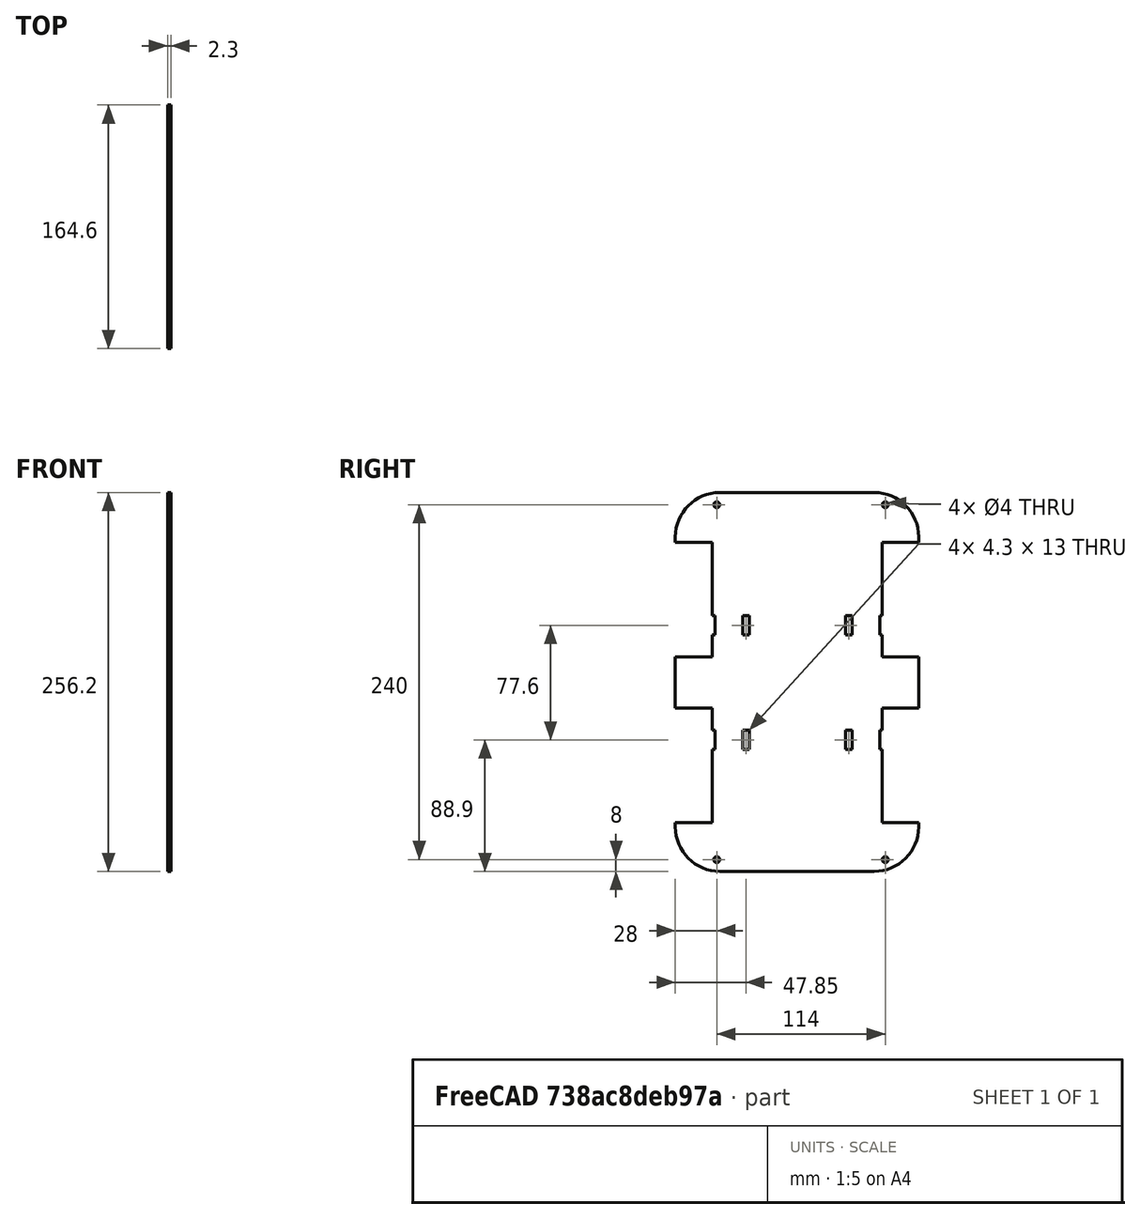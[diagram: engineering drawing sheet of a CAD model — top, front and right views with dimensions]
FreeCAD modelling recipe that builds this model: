
FCSTD DOCUMENT  (FreeCAD 0.17R13522 (Git))
Label: chasis_inferior
License: All rights reserved
LicenseURL: http://en.wikipedia.org/wiki/All_rights_reserved
objects: Part::Cut×16, Part::Box×13, Part::Fillet×4, Part::Cylinder×4
note: 37 computed .brp shape members not serialized (recipe doc carries the construction recipe); baked Part::Feature solids carry a one-line shape summary decoded from their .brp

FEATURE [Part::Box] Box  label="Cubo"
  AttacherType = Attacher::AttachEngine3D
  Height = 256.2
  Length = 2.3
  Width = 164.6
FEATURE [Part::Box] Box001  label="Cubo001"
  AttacherType = Attacher::AttachEngine3D
  Height = 77.4
  Length = 10
  Placement = pos=(0,0,33) rot=(0,0,1;0rad)
  Width = 25
FEATURE [Part::Box] Box002  label="Cubo002"
  AttacherType = Attacher::AttachEngine3D
  Height = 77.4
  Length = 10
  Placement = pos=(0,0,145) rot=(0,0,1;0rad)
  Width = 25
FEATURE [Part::Box] Box003  label="Cubo003"
  AttacherType = Attacher::AttachEngine3D
  Height = 77.4
  Length = 10
  Placement = pos=(0,140,33) rot=(0,0,1;0rad)
  Width = 25
FEATURE [Part::Cut] Cut
  Base = -> Box
  Tool = -> Box003
FEATURE [Part::Cut] Cut001
  Base = -> Cut
  Tool = -> Box001
FEATURE [Part::Box] Box004  label="Cubo004"
  AttacherType = Attacher::AttachEngine3D
  Height = 77.4
  Length = 10
  Placement = pos=(0,140,145) rot=(0,0,1;0rad)
  Width = 25
FEATURE [Part::Cut] Cut002
  Base = -> Cut001
  Tool = -> Box004
FEATURE [Part::Cut] Cut003
  Base = -> Cut002
  Tool = -> Box002
FEATURE [Part::Fillet] Fillet
  Base = -> Cut003
  Edges = 1 edges r=30: [Edge29]
FEATURE [Part::Fillet] Fillet001
  Base = -> Fillet
  Edges = 1 edges r=30: [Edge23]
FEATURE [Part::Fillet] Fillet002
  Base = -> Fillet001
  Edges = 1 edges r=30: [Edge63]
FEATURE [Part::Fillet] Fillet003
  Base = -> Fillet002
  Edges = 1 edges r=30: [Edge31]
FEATURE [Part::Box] Box005  label="Cubo005"
  AttacherType = Attacher::AttachEngine3D
  Height = 13
  Length = 10
  Placement = pos=(-2,25,82.4) rot=(0,0,1;0rad)
  Width = 1.8
FEATURE [Part::Box] Box006  label="Cubo006"
  AttacherType = Attacher::AttachEngine3D
  Height = 13
  Length = 10
  Placement = pos=(0,45.7,82.4) rot=(0,0,1;0rad)
  Width = 4.3
FEATURE [Part::Box] Box007  label="Cubo007"
  AttacherType = Attacher::AttachEngine3D
  Height = 13
  Length = 10
  Placement = pos=(-2,138.2,82.4) rot=(0,0,1;0rad)
  Width = 1.8
FEATURE [Part::Cut] Cut004
  Base = -> Fillet003
  Tool = -> Box005
FEATURE [Part::Box] Box008  label="Cubo008"
  AttacherType = Attacher::AttachEngine3D
  Height = 13
  Length = 10
  Placement = pos=(0,45.7,160) rot=(0,0,1;0rad)
  Width = 4.3
FEATURE [Part::Cut] Cut005
  Base = -> Cut004
  Tool = -> Box006
FEATURE [Part::Box] Box009  label="Cubo009"
  AttacherType = Attacher::AttachEngine3D
  Height = 13
  Length = 10
  Placement = pos=(-2,115.2,82.4) rot=(0,0,1;0rad)
  Width = 4.3
FEATURE [Part::Box] Box010  label="Cubo010"
  AttacherType = Attacher::AttachEngine3D
  Height = 13
  Length = 10
  Placement = pos=(-2,25,160) rot=(0,0,1;0rad)
  Width = 1.8
FEATURE [Part::Cut] Cut006
  Base = -> Cut005
  Tool = -> Box010
FEATURE [Part::Cut] Cut007
  Base = -> Cut006
  Tool = -> Box008
FEATURE [Part::Box] Box011  label="Cubo011"
  AttacherType = Attacher::AttachEngine3D
  Height = 13
  Length = 10
  Placement = pos=(-2,138.2,160) rot=(0,0,1;0rad)
  Width = 1.8
FEATURE [Part::Box] Box012  label="Cubo012"
  AttacherType = Attacher::AttachEngine3D
  Height = 13
  Length = 10
  Placement = pos=(-2,115.2,160) rot=(0,0,1;0rad)
  Width = 4.3
FEATURE [Part::Cut] Cut008
  Base = -> Cut007
  Tool = -> Box009
FEATURE [Part::Cut] Cut009
  Base = -> Cut008
  Tool = -> Box007
FEATURE [Part::Cut] Cut010
  Base = -> Cut009
  Tool = -> Box011
FEATURE [Part::Cut] Cut011
  Base = -> Cut010
  Tool = -> Box012
FEATURE [Part::Cylinder] Cylinder  label="Cilindro"
  Angle = 360
  AttacherType = Attacher::AttachEngine3D
  Height = 10
  Placement = pos=(-2,28,8) rot=(0,1,0;1.5708rad)
  Radius = 2
FEATURE [Part::Cylinder] Cylinder001  label="Cilindro001"
  Angle = 360
  AttacherType = Attacher::AttachEngine3D
  Height = 10
  Placement = pos=(-1,142,8) rot=(0,1,0;1.5708rad)
  Radius = 2
FEATURE [Part::Cylinder] Cylinder002  label="Cilindro002"
  Angle = 360
  AttacherType = Attacher::AttachEngine3D
  Height = 10
  Placement = pos=(-2,28,248) rot=(0,1,0;1.5708rad)
  Radius = 2
FEATURE [Part::Cylinder] Cylinder003  label="Cilindro003"
  Angle = 360
  AttacherType = Attacher::AttachEngine3D
  Height = 10
  Placement = pos=(-2,142,248) rot=(0,1,0;1.5708rad)
  Radius = 2
FEATURE [Part::Cut] Cut012
  Base = -> Cut011
  Tool = -> Cylinder
FEATURE [Part::Cut] Cut013
  Base = -> Cut012
  Tool = -> Cylinder001
FEATURE [Part::Cut] Cut014
  Base = -> Cut013
  Tool = -> Cylinder003
FEATURE [Part::Cut] Cut015
  Base = -> Cut014
  Tool = -> Cylinder002
